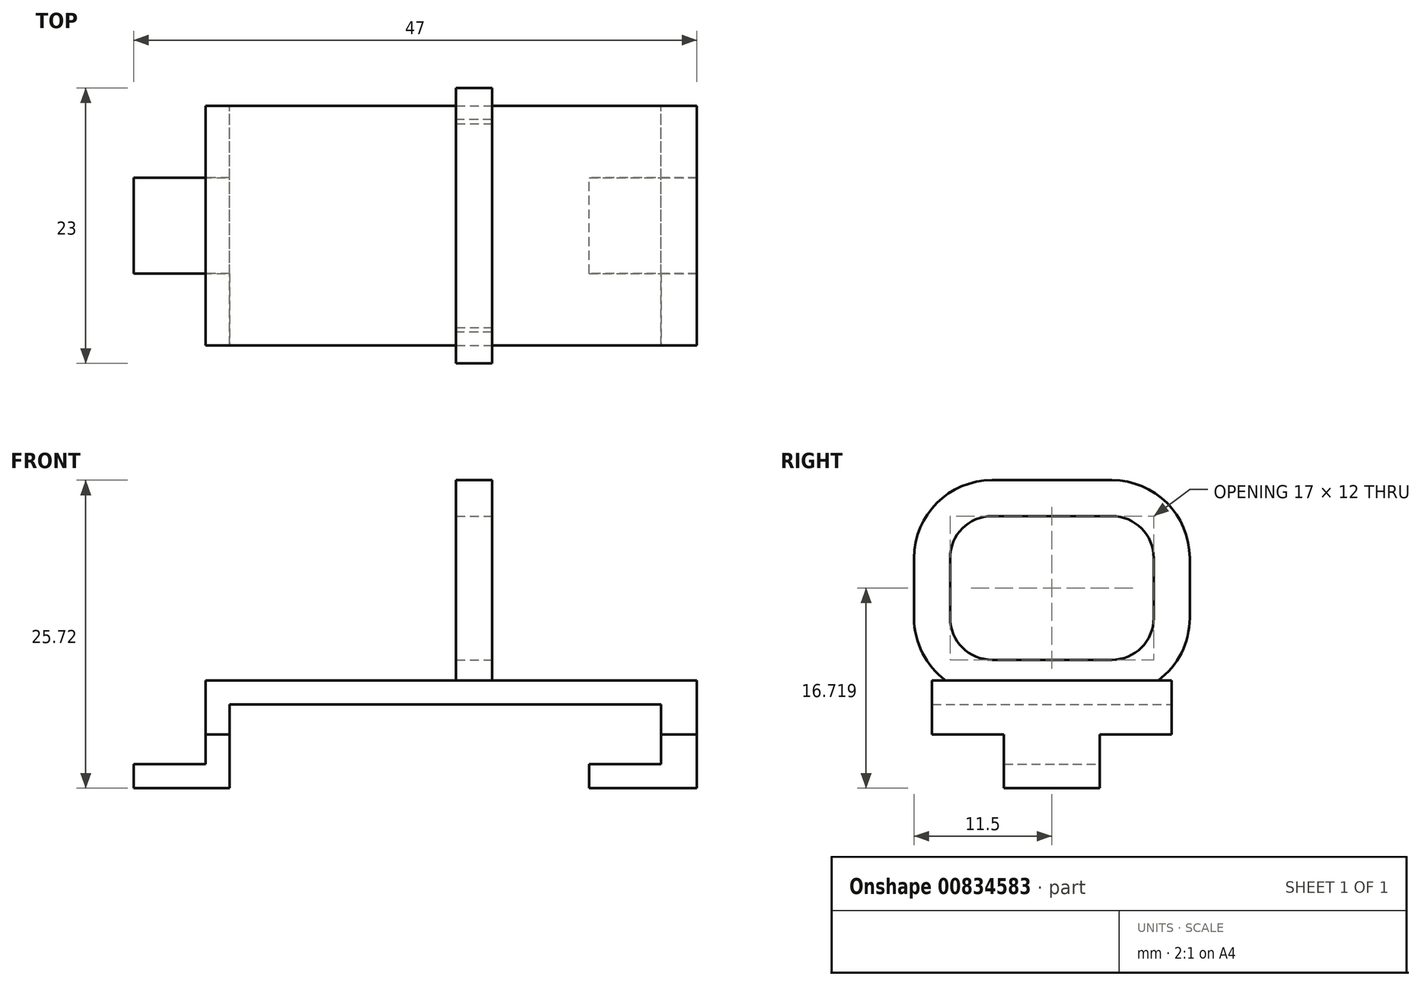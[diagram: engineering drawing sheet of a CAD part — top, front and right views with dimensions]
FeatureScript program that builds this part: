
annotation { "Feature Type Name" : "Feature", "Feature Type Description" : "" }
export const myFeature = defineFeature(function(context is Context, id is Id, definition is map)
    precondition{}
    {
        {
            var Q0;
            Q0=qCreatedBy(makeId("Front.planeOp"),FACE);
            var sketch = newSketch(context, id + "F0", { "sketchPlane" : qUnion([Q0])});
            skLineSegment(sketch, "E0", {"start": v(-28.4, 0) * mm, "end": v(-22.4, 0) * mm});
            skLineSegment(sketch, "E1", {"start": v(-22.4, 0) * mm, "end": v(-22.4, 7) * mm});
            skLineSegment(sketch, "E2", {"start": v(-22.4, 7) * mm, "end": v(18.6, 7) * mm});
            skLineSegment(sketch, "E3.0", {"start": v(-20.4, 5) * mm, "end": v(13.6, 5) * mm});
            skLineSegment(sketch, "E3.1", {"start": v(-20.4, -2) * mm, "end": v(-20.4, 5) * mm});
            skLineSegment(sketch, "E3.2", {"start": v(-28.4, -2) * mm, "end": v(-20.4, -2) * mm});
            skLineSegment(sketch, "E4", {"start": v(18.6, 7) * mm, "end": v(18.6, -2) * mm});
            skLineSegment(sketch, "E5", {"start": v(18.6, -2) * mm, "end": v(9.6, -2) * mm});
            skLineSegment(sketch, "E6", {"start": v(9.6, -2) * mm, "end": v(9.6, 0) * mm});
            skLineSegment(sketch, "E7", {"start": v(9.6, 0) * mm, "end": v(15.6, 0) * mm});
            skLineSegment(sketch, "E8", {"start": v(15.6, 0) * mm, "end": v(15.6, 5) * mm});
            skLineSegment(sketch, "E9", {"start": v(15.6, 5) * mm, "end": v(13.6, 5) * mm});
            skLineSegment(sketch, "E10", {"start": v(-28.4, -2) * mm, "end": v(-28.4, 0) * mm});
            skSolve(sketch);
        }
        {
            var Q0;
            Q0=makeQuery(id+"F0.imprint","IMPRINT",FACE,{"disambiguationData":[TD([[makeQuery(id+"F0.imprint","IMPRINT",EDGE,{"derivedFrom":sQuery(id+"F0.wireOp",EDGE,"E0")}),-1.0]])]});
            extrude(context, id + "F1", {"entities" : qUnion([Q0]), "depth" : 10 * mm, "offsetDistance" : 25 * mm});
        }
        {
            var Q0;
            Q0=makeQuery(id+"F1.opExtrude","CAP_FACE",FACE,{"disambiguationData":[OSD([sQuery(id+"F0.wireOp",EDGE,"E0"),sQuery(id+"F0.wireOp",EDGE,"E1"),sQuery(id+"F0.wireOp",EDGE,"E2"),sQuery(id+"F0.wireOp",EDGE,"E3.0"),sQuery(id+"F0.wireOp",EDGE,"E3.1"),sQuery(id+"F0.wireOp",EDGE,"E3.2"),sQuery(id+"F0.wireOp",EDGE,"E4"),sQuery(id+"F0.wireOp",EDGE,"E5"),sQuery(id+"F0.wireOp",EDGE,"E6"),sQuery(id+"F0.wireOp",EDGE,"E7"),sQuery(id+"F0.wireOp",EDGE,"E8"),sQuery(id+"F0.wireOp",EDGE,"E9"),sQuery(id+"F0.wireOp",EDGE,"E10")])],"isStart":false});
            var sketch = newSketch(context, id + "F2", { "sketchPlane" : qUnion([Q0])});
            skLineSegment(sketch, "E11", {"start": v(-22.4, 0) * mm, "end": v(-20.4, 0) * mm});
            skLineSegment(sketch, "E12", {"start": v(15.6, 0) * mm, "end": v(18.6, 0) * mm});
            skLineSegment(sketch, "E13", {"start": v(15.6, 2.5) * mm, "end": v(18.6, 2.5) * mm});
            skLineSegment(sketch, "E14", {"start": v(-20.4, 2.5) * mm, "end": v(-22.4, 2.5) * mm});
            skSolve(sketch);
        }
        {
            var Q0;
            Q0=qSketchRegion(id+"F2",true);
            var Q1;
            {var subQ0=sQuery(id+"F2.wireOp",EDGE,"E11");Q1=makeQuery(id+"F2.imprint","IMPRINT",FACE,{"disambiguationData":[TD([[makeQuery(id+"F2.imprint","IMPRINT",EDGE,{"derivedFrom":subQ0}),-1.0]])]});}
            var Q2;
            {var subQ1=sQuery(id+"F2.wireOp",EDGE,"E12");Q2=makeQuery(id+"F2.imprint","IMPRINT",FACE,{"disambiguationData":[TD([[makeQuery(id+"F2.imprint","IMPRINT",EDGE,{"derivedFrom":subQ1}),-1.0]])]});}
            extrude(context, id + "F3", {"entities" : qUnion([Q0, Q1, Q2]), "operationType" : NewBodyOperationType.REMOVE, "oppositeDirection" : true, "depth" : 6 * mm, "offsetDistance" : 25 * mm});
        }
        {
            var Q0;
            {var subQ0=sQuery(id+"F2.wireOp",EDGE,"E11");Q0=makeQuery(id+"F2.imprint","IMPRINT",FACE,{"disambiguationData":[TD([[makeQuery(id+"F2.imprint","IMPRINT",EDGE,{"derivedFrom":subQ0}),1.0]])]});}
            var Q1;
            {var subQ0=sQuery(id+"F2.wireOp",EDGE,"E12");Q1=makeQuery(id+"F2.imprint","IMPRINT",FACE,{"disambiguationData":[TD([[makeQuery(id+"F2.imprint","IMPRINT",EDGE,{"derivedFrom":subQ0}),1.0]])]});}
            extrude(context, id + "F4", {"entities" : qUnion([Q0, Q1]), "operationType" : NewBodyOperationType.REMOVE, "oppositeDirection" : true, "depth" : 6 * mm, "offsetDistance" : 25 * mm});
        }
        {
            var Q0;
            Q0=qCreatedBy(makeId("Right.planeOp"),FACE);
            var sketch = newSketch(context, id + "F5", { "sketchPlane" : qUnion([Q0])});
            skLineSegment(sketch, "E15", {"start": v(0, 7.22) * mm, "end": v(-5, 7.22) * mm});
            skLineSegment(sketch, "E16", {"start": v(-10, 12.22) * mm, "end": v(-10, 17.22) * mm});
            skPoint(sketch, "E17.visualSharp", {"position": v(-10, 7.22) * mm});
            skArc(sketch, "E17.filletArc", {"start": v(-10, 12.22) * mm, "mid": v(-8.54, 8.68) * mm, "end": v(-5, 7.22) * mm});
            skLineSegment(sketch, "E18", {"start": v(-5, 22.22) * mm, "end": v(0, 22.22) * mm});
            skPoint(sketch, "E19.visualSharp", {"position": v(-10, 22.22) * mm});
            skArc(sketch, "E19.filletArc", {"start": v(-5, 22.22) * mm, "mid": v(-8.54, 20.75) * mm, "end": v(-10, 17.22) * mm});
            skSolve(sketch);
        }
        {
            var Q0;
            Q0=qCreatedBy(makeId("Front.planeOp"),FACE);
            var sketch = newSketch(context, id + "F6", { "sketchPlane" : qUnion([Q0])});
            skLineSegment(sketch, "E20.bottom", {"start": v(-1.5, 5.72) * mm, "end": v(1.5, 5.72) * mm});
            skLineSegment(sketch, "E20.top", {"start": v(-1.5, 8.72) * mm, "end": v(1.5, 8.72) * mm});
            skLineSegment(sketch, "E20.left", {"start": v(-1.5, 5.72) * mm, "end": v(-1.5, 8.72) * mm});
            skLineSegment(sketch, "E20.right", {"start": v(1.5, 5.72) * mm, "end": v(1.5, 8.72) * mm});
            skPoint(sketch, "E20.middle", {"position": v(0, 7.22) * mm});
            skSolve(sketch);
        }
        {
            var Q0;
            Q0=makeQuery(id+"F6.imprint","IMPRINT",FACE,{"disambiguationData":[TD([[makeQuery(id+"F6.imprint","IMPRINT",EDGE,{"derivedFrom":sQuery(id+"F6.wireOp",EDGE,"E20.bottom")}),1.0]])]});
            var Q1;
            Q1=sQuery(id+"F5.wireOp",EDGE,"E15");
            var Q2;
            Q2=sQuery(id+"F5.wireOp",EDGE,"E17.filletArc");
            var Q3;
            Q3=sQuery(id+"F5.wireOp",EDGE,"E19.filletArc");
            var Q4;
            Q4=sQuery(id+"F5.wireOp",EDGE,"E18");
            var Q5;
            Q5=sQuery(id+"F5.wireOp",EDGE,"E16");
            sweep(context, id + "F7", {"operationType" : NewBodyOperationType.ADD, "profiles" : qUnion([Q0]), "path" : qUnion([Q1, Q2, Q3, Q4, Q5])});
        }
        {
            var Q0;
            Q0=makeQuery(id+"F1.opExtrude","SWEPT_BODY",BODY,{"disambiguationData":[OSD([sQuery(id+"F0.wireOp",EDGE,"E0"),sQuery(id+"F0.wireOp",EDGE,"E1"),sQuery(id+"F0.wireOp",EDGE,"E2"),sQuery(id+"F0.wireOp",EDGE,"E3.0"),sQuery(id+"F0.wireOp",EDGE,"E3.1"),sQuery(id+"F0.wireOp",EDGE,"E3.2"),sQuery(id+"F0.wireOp",EDGE,"E4"),sQuery(id+"F0.wireOp",EDGE,"E5"),sQuery(id+"F0.wireOp",EDGE,"E6"),sQuery(id+"F0.wireOp",EDGE,"E7"),sQuery(id+"F0.wireOp",EDGE,"E8"),sQuery(id+"F0.wireOp",EDGE,"E9"),sQuery(id+"F0.wireOp",EDGE,"E10")])]});
            var Q1;
            Q1=qCreatedBy(makeId("Front.planeOp"),FACE);
            mirror(context, id + "F8", {"operationType" : NewBodyOperationType.ADD, "entities" : qUnion([Q0]), "mirrorPlane" : qUnion([Q1])});
        }
    });
